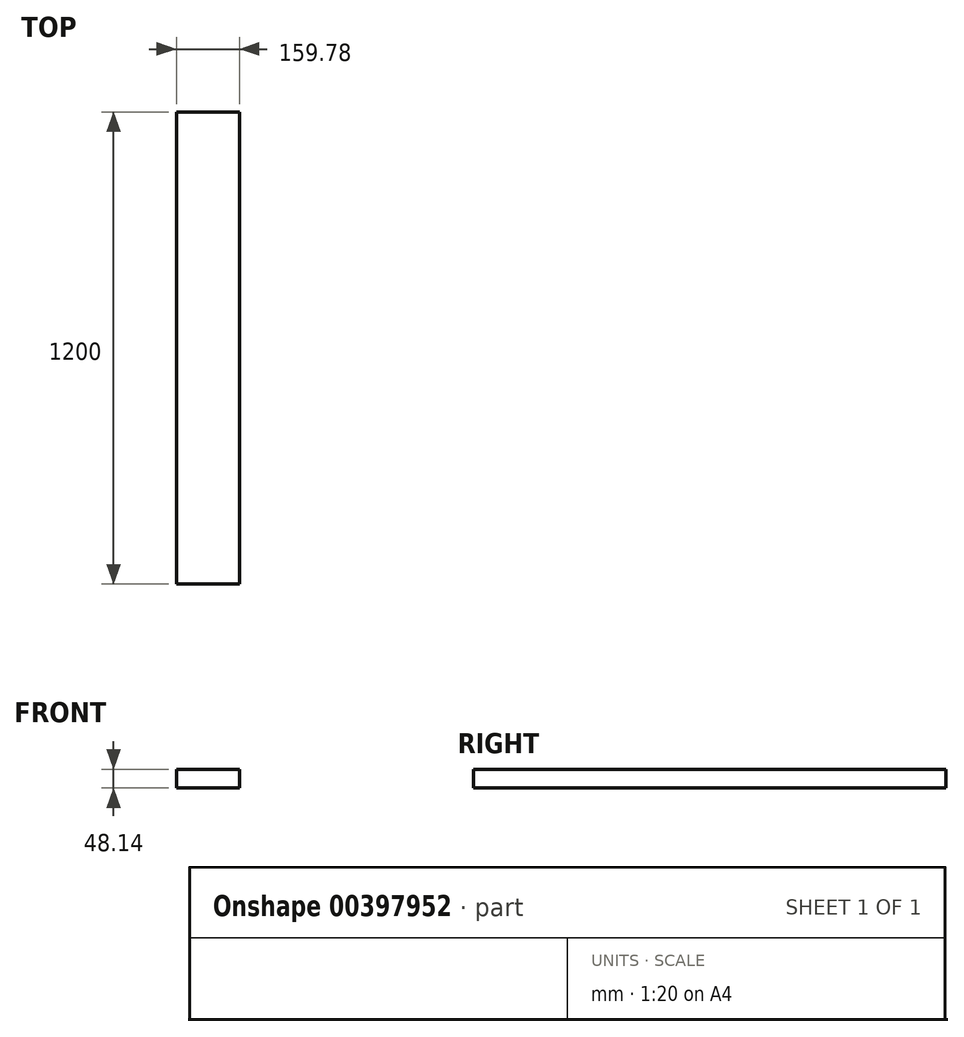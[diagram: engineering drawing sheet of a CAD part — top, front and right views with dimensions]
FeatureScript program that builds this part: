
annotation { "Feature Type Name" : "Feature", "Feature Type Description" : "" }
export const myFeature = defineFeature(function(context is Context, id is Id, definition is map)
    precondition{}
    {
        {
            var Q0;
            Q0=qCreatedBy(makeId("Front.planeOp"),FACE);
            var sketch = newSketch(context, id + "F0", { "sketchPlane" : qUnion([Q0])});
            skLineSegment(sketch, "E0.bottom", {"start": v(79.9, -24.07) * mm, "end": v(-79.9, -24.07) * mm});
            skLineSegment(sketch, "E0.top", {"start": v(79.9, 24.07) * mm, "end": v(-79.9, 24.07) * mm});
            skLineSegment(sketch, "E0.left", {"start": v(79.9, -24.07) * mm, "end": v(79.9, 24.07) * mm});
            skLineSegment(sketch, "E0.right", {"start": v(-79.9, -24.07) * mm, "end": v(-79.9, 24.07) * mm});
            skPoint(sketch, "E0.middle", {"position": v(0, 0) * mm});
            skSolve(sketch);
        }
        {
            var Q0;
            Q0 = qSketchRegion(id + "F0", true);
            extrude(context, id + "F1", {"entities" : qUnion([Q0]), "depth" : 1200 * mm, "offsetDistance" : 25.4 * mm});
        }
    });
